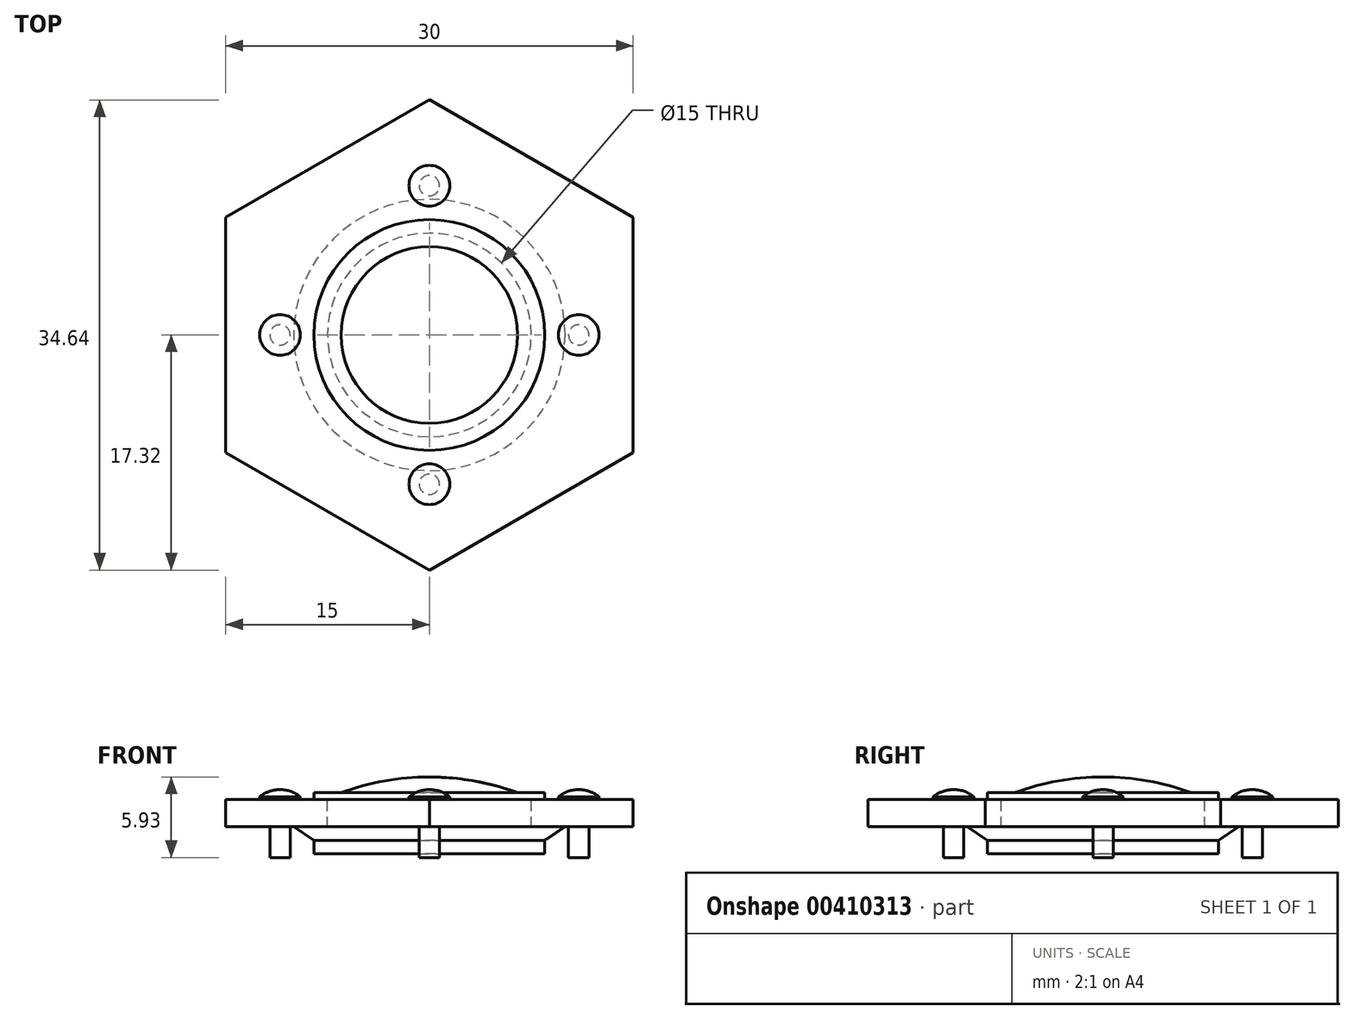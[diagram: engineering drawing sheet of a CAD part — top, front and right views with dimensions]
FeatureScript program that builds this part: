
annotation { "Feature Type Name" : "Feature", "Feature Type Description" : "" }
export const myFeature = defineFeature(function(context is Context, id is Id, definition is map)
    precondition{}
    {
        {
            var Q0;
            Q0=qCreatedBy(makeId("Top.planeOp"),FACE);
            var sketch = newSketch(context, id + "F0", { "sketchPlane" : qUnion([Q0])});
            skCircle(sketch, "E0.cCircle", {"center": v(0, 0) * mm, "radius": 15 * mm, "construction": true});
            skLineSegment(sketch, "E0.0", {"start": v(15, 8.66) * mm, "end": v(15, -8.66) * mm});
            skLineSegment(sketch, "E0.1", {"start": v(15, -8.66) * mm, "end": v(0, -17.32) * mm});
            skLineSegment(sketch, "E0.2", {"start": v(0, -17.32) * mm, "end": v(-15, -8.66) * mm});
            skLineSegment(sketch, "E0.3", {"start": v(-15, -8.66) * mm, "end": v(-15, 8.66) * mm});
            skLineSegment(sketch, "E0.4", {"start": v(-15, 8.66) * mm, "end": v(0, 17.32) * mm});
            skLineSegment(sketch, "E0.5", {"start": v(0, 17.32) * mm, "end": v(15, 8.66) * mm});
            skPoint(sketch, "E0.0.midPoint", {"position": v(15, 0) * mm});
            skCircle(sketch, "E1", {"center": v(11, 0) * mm, "radius": 0.75 * mm});
            skCircle(sketch, "E2.1.0", {"center": v(0, 11) * mm, "radius": 0.75 * mm});
            skCircle(sketch, "E2.2.0", {"center": v(-11, 0) * mm, "radius": 0.75 * mm});
            skCircle(sketch, "E2.3.0", {"center": v(0, -11) * mm, "radius": 0.75 * mm});
            skCircle(sketch, "E3", {"center": v(0, 0) * mm, "radius": 7.5 * mm});
            skSolve(sketch);
        }
        {
            var Q0;
            Q0 = qSketchRegion(id + "F0", true);
            extrude(context, id + "F1", {"entities" : qUnion([Q0]), "depth" : 2 * mm});
        }
        {
            var Q0;
            Q0=qCreatedBy(makeId("Front.planeOp"),FACE);
            var sketch = newSketch(context, id + "F2", { "sketchPlane" : qUnion([Q0])});
            skLineSegment(sketch, "E4", {"start": v(8.5, 2.5) * mm, "end": v(8.5, 2) * mm});
            skLineSegment(sketch, "E5", {"start": v(8.5, 2) * mm, "end": v(7.5, 2) * mm});
            skLineSegment(sketch, "E6", {"start": v(7.5, 2) * mm, "end": v(7.5, 0) * mm});
            skLineSegment(sketch, "E7", {"start": v(7.5, 0) * mm, "end": v(10, 0) * mm});
            skLineSegment(sketch, "E8", {"start": v(10, 0) * mm, "end": v(8.5, -1) * mm});
            skLineSegment(sketch, "E9", {"start": v(8.5, -1) * mm, "end": v(8.5, -2) * mm});
            skLineSegment(sketch, "E10", {"start": v(8.5, -2) * mm, "end": v(0, -2) * mm});
            skLineSegment(sketch, "E11", {"start": v(8.5, 2.5) * mm, "end": v(6.5, 2.5) * mm});
            skLineSegment(sketch, "E12", {"start": v(0, 3.66) * mm, "end": v(0, -2) * mm});
            skArc(sketch, "E13", {"start": v(6.5, 2.5) * mm, "mid": v(3.3, 3.37) * mm, "end": v(0, 3.66) * mm});
            skSolve(sketch);
        }
        {
            var Q0;
            Q0 = qSketchRegion(id + "F2", true);
            var Q1;
            Q1=sQuery(id+"F2.wireOp",EDGE,"E12");
            revolve(context, id + "F3", {"entities" : qUnion([Q0]), "axis" : qUnion([Q1]), "revolveType" : RevolveType.FULL});
        }
        {
            var Q0;
            Q0=qCreatedBy(makeId("Front.planeOp"),FACE);
            var sketch = newSketch(context, id + "F4", { "sketchPlane" : qUnion([Q0])});
            skLineSegment(sketch, "E14", {"start": v(12.5, 2.2) * mm, "end": v(12.5, 2) * mm});
            skLineSegment(sketch, "E15", {"start": v(12.5, 2) * mm, "end": v(11.75, 2) * mm});
            skLineSegment(sketch, "E16", {"start": v(11.75, 2) * mm, "end": v(11.75, -2.27) * mm});
            skLineSegment(sketch, "E17", {"start": v(11.75, -2.27) * mm, "end": v(11, -2.27) * mm});
            skLineSegment(sketch, "E18", {"start": v(11, -2.27) * mm, "end": v(11, 2.73) * mm});
            skLineSegment(sketch, "E19", {"start": v(0, 15.34) * mm, "end": v(0, -13.6) * mm});
            skArc(sketch, "E20", {"start": v(12.5, 2.2) * mm, "mid": v(11.8, 2.6) * mm, "end": v(11, 2.73) * mm});
            skSolve(sketch);
        }
        {
            var Q0;
            Q0=makeQuery(id+"F4.imprint","IMPRINT",FACE,{"disambiguationData":[TD([[makeQuery(id+"F4.imprint","IMPRINT",EDGE,{"derivedFrom":sQuery(id+"F4.wireOp",EDGE,"E14")}),-1.0]])]});
            var Q1;
            Q1=sQuery(id+"F4.wireOp",EDGE,"E18");
            revolve(context, id + "F5", {"entities" : qUnion([Q0]), "axis" : qUnion([Q1]), "revolveType" : RevolveType.FULL});
        }
        {
            var Q0;
            Q0=makeQuery(id+"F5.opRevolve","SWEPT_BODY",BODY,{"disambiguationData":[OSD([sQuery(id+"F4.wireOp",EDGE,"MYAO5i1J-qb6L-lJWI-d8I6-xIFWZ9uoy0KC"),sQuery(id+"F4.wireOp",EDGE,"E14"),sQuery(id+"F4.wireOp",EDGE,"E15"),sQuery(id+"F4.wireOp",EDGE,"E16"),sQuery(id+"F4.wireOp",EDGE,"E17"),sQuery(id+"F4.wireOp",EDGE,"E18")])]});
            var Q1;
            Q1=sQuery(id+"F4.wireOp",EDGE,"E19");
            circularPattern(context, id + "F6", {"operationType" : NewBodyOperationType.ADD, "entities" : qUnion([Q0]), "axis" : qUnion([Q1]), "angle" : 360 * degree, "instanceCount" : 4, "equalSpace" : true});
        }
    });
